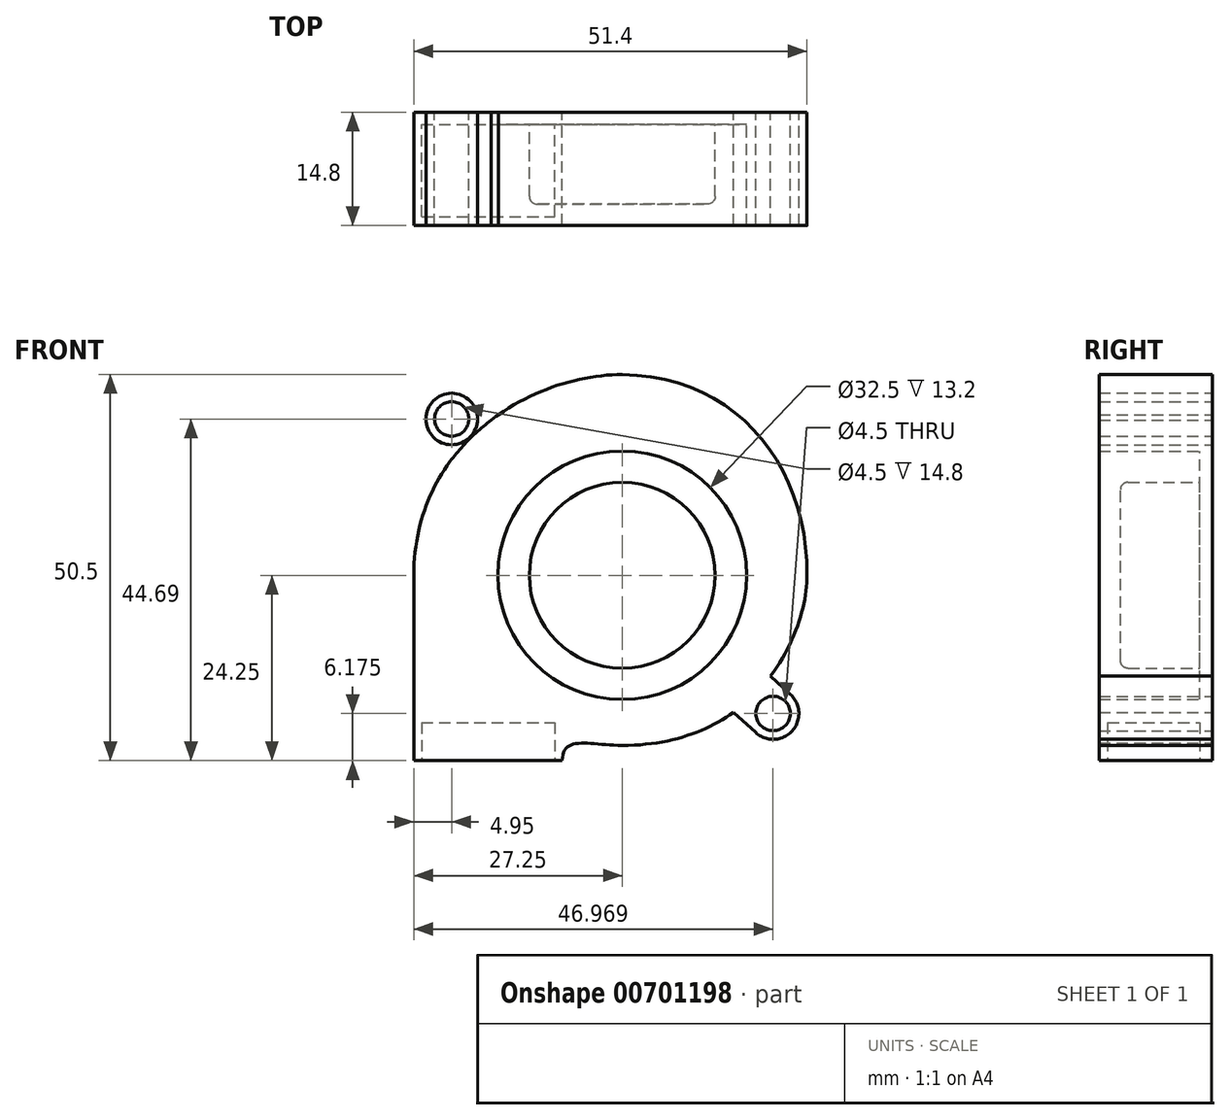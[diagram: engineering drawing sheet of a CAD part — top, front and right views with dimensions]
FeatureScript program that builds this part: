
annotation { "Feature Type Name" : "Feature", "Feature Type Description" : "" }
export const myFeature = defineFeature(function(context is Context, id is Id, definition is map)
    precondition{}
    {
        {
            var Q0;
            Q0=qCreatedBy(makeId("Front.planeOp"),FACE);
            var sketch = newSketch(context, id + "F0", { "sketchPlane" : qUnion([Q0])});
            skCircle(sketch, "E0", {"center": v(0, 0) * mm, "radius": 12.15 * mm});
            skLineSegment(sketch, "E1", {"start": v(-27.25, -24.25) * mm, "end": v(-7.85, -24.25) * mm});
            skLineSegment(sketch, "E2", {"start": v(-27.25, -24.25) * mm, "end": v(-27.25, 26.58) * mm, "construction": true});
            skCircle(sketch, "E3", {"center": v(0, 0) * mm, "radius": 16.25 * mm});
            skLineSegment(sketch, "E4", {"start": v(0, -16.25) * mm, "end": v(0, -22.25) * mm, "construction": true});
            skLineSegment(sketch, "E5", {"start": v(-28.82, -22.25) * mm, "end": v(28.82, -22.25) * mm, "construction": true});
            skLineSegment(sketch, "E6", {"start": v(-16.25, 0) * mm, "end": v(-27.25, 0) * mm, "construction": true});
            skLineSegment(sketch, "E7", {"start": v(-27.25, 8.4) * mm, "end": v(-27.25, -8.4) * mm, "construction": true});
            skLineSegment(sketch, "E8", {"start": v(-27.25, -24.25) * mm, "end": v(-27.25, 0) * mm});
            skLineSegment(sketch, "E9", {"start": v(-22.3, 20.44) * mm, "end": v(19.72, -18.07) * mm, "construction": true});
            skLineSegment(sketch, "E10", {"start": v(16.25, 0) * mm, "end": v(24.15, 0) * mm, "construction": true});
            skLineSegment(sketch, "E11", {"start": v(0, 16.25) * mm, "end": v(0, 26.25) * mm});
            skFitSpline(sketch, "E12", {"points": [v(24.15, 0) * mm, v(0, 26.25) * mm], "startDerivative": vector(0.43, 42.98) * mm, "endDerivative": vector(-44.69, 0.53) * mm});
            skFitSpline(sketch, "E13", {"points": [v(0, 26.25) * mm, v(-27.25, 0) * mm], "startDerivative": vector(-34.53, 0.09) * mm, "endDerivative": vector(0, -52.28) * mm});
            skCircle(sketch, "E14", {"center": v(0, 0) * mm, "radius": 26.25 * mm, "construction": true});
            skCircle(sketch, "E15", {"center": v(19.72, -18.07) * mm, "radius": 3.38 * mm});
            skCircle(sketch, "E16", {"center": v(-22.3, 20.44) * mm, "radius": 3.38 * mm});
            skLineSegment(sketch, "E17", {"start": v(-7.85, -24.25) * mm, "end": v(40.7, -24.25) * mm, "construction": true});
            skFitSpline(sketch, "E18", {"points": [v(24.15, 0) * mm, v(0, -22.25) * mm], "startDerivative": vector(0, -23.58) * mm, "endDerivative": vector(-52.82, 0) * mm});
            skLineSegment(sketch, "E19", {"start": v(24.15, 0) * mm, "end": v(24.15, -18.3) * mm, "construction": true});
            skFitSpline(sketch, "E20", {"points": [v(-7.85, -24.25) * mm, v(0, -22.25) * mm], "startDerivative": vector(0.1, 10.3) * mm, "endDerivative": vector(13.01, 0) * mm});
            skCircle(sketch, "E21", {"center": v(-22.3, 20.44) * mm, "radius": 2.25 * mm});
            skCircle(sketch, "E22", {"center": v(19.72, -18.07) * mm, "radius": 2.25 * mm});
            skLineSegment(sketch, "E23", {"start": v(22, -15.59) * mm, "end": v(19.38, -13.19) * mm});
            skLineSegment(sketch, "E24", {"start": v(17.44, -20.56) * mm, "end": v(14.54, -17.9) * mm});
            skLineSegment(sketch, "E25", {"start": v(-24.58, 17.95) * mm, "end": v(-22.66, 16.19) * mm});
            skLineSegment(sketch, "E26", {"start": v(-20.02, 22.93) * mm, "end": v(-17.75, 20.85) * mm});
            skArc(sketch, "E27.filletArc", {"start": v(-22.52, 14.86) * mm, "mid": v(-22.34, 15.55) * mm, "end": v(-22.66, 16.19) * mm});
            skFitSpline(sketch, "E28", {"points": [v(0, 26.25) * mm, v(-17.15, 20.3) * mm], "startDerivative": vector(-26.98, 0.09) * mm, "endDerivative": vector(-10.48, -7.64) * mm});
            skArc(sketch, "E29.filletArc", {"start": v(-17.75, 20.85) * mm, "mid": v(-17.13, 20.59) * mm, "end": v(-16.49, 20.77) * mm});
            skSolve(sketch);
        }
        {
            var Q0;
            Q0=makeQuery(id+"F0.imprint","IMPRINT",FACE,{"disambiguationData":[TD([[makeQuery(id+"F0.imprint","IMPRINT",EDGE,{"derivedFrom":sQuery(id+"F0.wireOp",EDGE,"E1")}),1.0]])]});
            var Q1;
            Q1=makeQuery(id+"F0.imprint","IMPRINT",FACE,{"disambiguationData":[TD([[makeQuery(id+"F0.imprint","IMPRINT",EDGE,{"derivedFrom":sQuery(id+"F0.wireOp",EDGE,"E21")}),-1.0]])]});
            var Q2;
            Q2=makeQuery(id+"F0.imprint","IMPRINT",FACE,{"disambiguationData":[TD([[makeQuery(id+"F0.imprint","IMPRINT",EDGE,{"derivedFrom":sQuery(id+"F0.wireOp",EDGE,"E22")}),-1.0]])]});
            var Q3;
            {var subQ0=sQuery(id+"F0.wireOp",EDGE,"E23");Q3=makeQuery(id+"F0.imprint","IMPRINT",FACE,{"disambiguationData":[TD([[makeQuery(id+"F0.imprint","IMPRINT",EDGE,{"derivedFrom":subQ0}),1.0]])]});}
            extrude(context, id + "F1", {"entities" : qUnion([Q0, Q1, Q2, Q3]), "depth" : 14.8 * mm, "offsetDistance" : 25 * mm});
        }
        {
            var Q0;
            Q0=makeQuery(id+"F0.imprint","IMPRINT",FACE,{"disambiguationData":[TD([[makeQuery(id+"F0.imprint","IMPRINT",EDGE,{"derivedFrom":sQuery(id+"F0.wireOp",EDGE,"E21")}),-1.0]])]});
            var Q1;
            Q1=makeQuery(id+"F0.imprint","IMPRINT",FACE,{"disambiguationData":[TD([[makeQuery(id+"F0.imprint","IMPRINT",EDGE,{"derivedFrom":sQuery(id+"F0.wireOp",EDGE,"E1")}),1.0]])]});
            var Q2;
            Q2=makeQuery(id+"F0.imprint","IMPRINT",FACE,{"disambiguationData":[TD([[makeQuery(id+"F0.imprint","IMPRINT",EDGE,{"derivedFrom":sQuery(id+"F0.wireOp",EDGE,"E0")}),1.0]])]});
            var Q3;
            Q3=makeQuery(id+"F0.imprint","IMPRINT",FACE,{"disambiguationData":[TD([[makeQuery(id+"F0.imprint","IMPRINT",EDGE,{"derivedFrom":sQuery(id+"F0.wireOp",EDGE,"E0")}),-1.0]])]});
            var Q4;
            {var subQ0=sQuery(id+"F0.wireOp",EDGE,"E23");Q4=makeQuery(id+"F0.imprint","IMPRINT",FACE,{"disambiguationData":[TD([[makeQuery(id+"F0.imprint","IMPRINT",EDGE,{"derivedFrom":subQ0}),1.0]])]});}
            var Q5;
            Q5=makeQuery(id+"F0.imprint","IMPRINT",FACE,{"disambiguationData":[TD([[makeQuery(id+"F0.imprint","IMPRINT",EDGE,{"derivedFrom":sQuery(id+"F0.wireOp",EDGE,"E22")}),-1.0]])]});
            extrude(context, id + "F2", {"entities" : qUnion([Q0, Q1, Q2, Q3, Q4, Q5]), "operationType" : NewBodyOperationType.ADD, "depth" : 1.6 * mm, "offsetDistance" : 25 * mm});
        }
        {
            var Q0;
            Q0=makeQuery(id+"F0.imprint","IMPRINT",FACE,{"disambiguationData":[TD([[makeQuery(id+"F0.imprint","IMPRINT",EDGE,{"derivedFrom":sQuery(id+"F0.wireOp",EDGE,"E0")}),1.0]])]});
            extrude(context, id + "F3", {"entities" : qUnion([Q0]), "operationType" : NewBodyOperationType.ADD, "depth" : 12 * mm, "offsetDistance" : 25 * mm});
        }
        {
            var Q0;
            Q0=makeQuery(id+"F3.opExtrude","CAP_EDGE",EDGE,{"disambiguationData":[OSD([sQuery(id+"F0.wireOp",EDGE,"E0")])],"isStart":false});
            fillet(context, id + "F4", {"entities" : qUnion([Q0]), "radius" : 1 * mm, "tangentPropagation" : true, "allowEdgeOverflow" : false});
        }
        {
            var Q0;
            Q0=makeQuery(id+"F1.opExtrude","SWEPT_FACE",FACE,{"disambiguationData":[OSD([sQuery(id+"F0.wireOp",EDGE,"E1")])]});
            var sketch = newSketch(context, id + "F5", { "sketchPlane" : qUnion([Q0])});
            skLineSegment(sketch, "E30.bottom", {"start": v(-26.25, 13.66) * mm, "end": v(-8.85, 13.66) * mm});
            skLineSegment(sketch, "E30.top", {"start": v(-26.25, 1.6) * mm, "end": v(-8.85, 1.6) * mm});
            skLineSegment(sketch, "E30.left", {"start": v(-26.25, 13.66) * mm, "end": v(-26.25, 1.6) * mm});
            skLineSegment(sketch, "E30.right", {"start": v(-8.85, 13.66) * mm, "end": v(-8.85, 1.6) * mm});
            skSolve(sketch);
        }
        {
            var Q0;
            Q0=makeQuery(id+"F5.imprint","IMPRINT",FACE,{"disambiguationData":[TD([[makeQuery(id+"F5.imprint","IMPRINT",EDGE,{"derivedFrom":sQuery(id+"F5.wireOp",EDGE,"E30.bottom")}),-1.0]])]});
            extrude(context, id + "F6", {"entities" : qUnion([Q0]), "operationType" : NewBodyOperationType.REMOVE, "oppositeDirection" : true, "depth" : 5 * mm, "offsetDistance" : 25 * mm});
        }
    });
